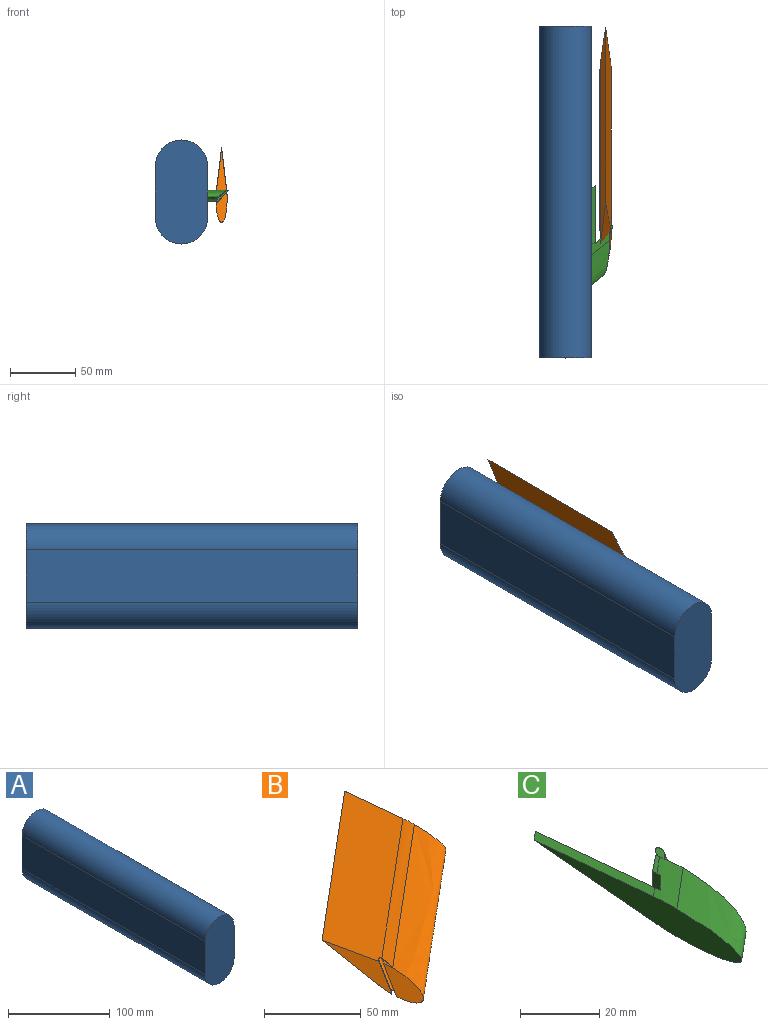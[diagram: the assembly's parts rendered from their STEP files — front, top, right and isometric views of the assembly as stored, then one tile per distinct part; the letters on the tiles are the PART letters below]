
ASSEMBLY  parts=3 mates=2
PART A: 6 faces, bbox 40x255x80 mm
  f0: plane 255x40mm, normal (1,0,0), area 10200mm2, adj f1,f3,f4,f5
  f1: cylinder r=20mm len=255mm, axis (0,1,0), area 16022.1mm2, adj f0,f2,f4,f5
  f2: plane 255x40mm, normal (-1,0,0), area 10200mm2, adj f1,f3,f4,f5
  f3: cylinder r=20mm len=255mm, axis (0,1,0), area 16022.1mm2, adj f0,f2,f4,f5
  f4: plane 80x40mm, normal (0,-1,0), area 2856.6mm2, adj f0,f1,f2,f3
  f5: plane 80x40mm, normal (0,1,0), area 2856.6mm2, adj f0,f1,f2,f3
PART B: 11 faces, bbox 107.4x163.4x11.2 mm
  f0: bspline ~112.18x107.25mm, area 5116.6mm2, adj f1,f2,f4,f5,f7,f8,f9,f10
  f1: bspline ~98.89x91.37mm, area 827.7mm2, adj f0,f2,f3,f4,f8,f9
  f2: plane 33.67x8.66mm, normal (-0.71,0,0.71), area 237.4mm2, adj f0,f1,f8
  f3: plane 124.24x102.95mm, normal (-0.08,0.09,0.99), area 4331.9mm2, adj f1,f4,f6,f7,f9,f10
  f4: plane 74.14x8.6mm, normal (1,0,0), area 393.1mm2, adj f0,f1,f3,f5,f6
  f5: bspline ~107.25x98.38mm, area 900.1mm2, adj f0,f4,f6,f7
  f6: plane 132.31x106.86mm, normal (-0.08,0.09,-0.99), area 4505.1mm2, adj f3,f4,f5,f7
  f7: plane 55.38x8.25mm, normal (-0.71,0,0.71), area 276.3mm2, adj f0,f3,f5,f6,f10
  f8: plane 19.29x9.68mm, normal (-0.59,0.55,-0.59), area 21.3mm2, adj f0,f1,f2,f9
  f9: cylinder r=1mm len=21.6mm, axis (0.39,0.84,0.39), area 65.9mm2, adj f0,f1,f3,f8,f10
  f10: plane 18.81x9.45mm, normal (0.59,-0.55,0.59), area 20.7mm2, adj f0,f3,f7,f9
PART C: 17 faces, bbox 16.7x99.9x11.4 mm
  f0: bspline ~19.96x13.79mm, area 106.4mm2, adj f1,f4,f6,f7,f8,f10,f12,f13
  f1: plane 45.16x3.92mm, normal (-0.08,0.09,0.99), area 128.8mm2, adj f0,f3,f8,f16
  f2: bspline ~19.96x13.79mm, area 40.5mm2, adj f3,f5,f7,f8,f15,f16
  f3: plane 45.16x3.92mm, normal (-0.08,0.09,-0.99), area 128.8mm2, adj f1,f2,f8,f16
  f4: plane 33.64x8.66mm, normal (0.71,0,-0.71), area 237.1mm2, adj f0,f7,f10
  f5: plane 19.01x8.34mm, normal (0.71,0,-0.71), area 67.9mm2, adj f2,f6,f7,f11,f13,f14,f15
  f6: plane 5.99x5.63mm, normal (-0.08,0.09,0.99), area 8.3mm2, adj f0,f5,f13,f14
  f7: bspline ~57.79x13.79mm, area 479.7mm2, adj f0,f2,f4,f5,f8,f10,f11
  f8: plane 74.14x8.6mm, normal (-1,0,0), area 393.1mm2, adj f0,f1,f2,f3,f7
  f9: plane 5x2.89mm, normal (-0.08,0.09,0.99), area 7.8mm2, adj f10,f11,f12
  f10: plane 18.8x9.43mm, normal (0.45,-0.54,0.71), area 17.4mm2, adj f0,f4,f7,f9,f11,f12
  f11: cylinder r=1mm len=21.9mm, axis (-0.39,-0.84,-0.39), area 99mm2, adj f5,f7,f9,f10
  f12: plane 1.77x0.16mm, normal (-0.8,0.1,0.59), area 0mm2, adj f0,f9,f10
  f13: plane 5.74x2.98mm, normal (-1,0,0), area 16.8mm2, adj f0,f5,f6,f14,f15
  f14: plane 5.5x5.5mm, normal (-0.62,0.78,0), area 19.3mm2, adj f5,f6,f13
  f15: plane 8.14x4.78mm, normal (-0.69,0.73,0), area 49.7mm2, adj f0,f2,f5,f13,f16
  f16: plane 44.56x8.14mm, normal (1,0,0), area 182.3mm2, adj f0,f1,f2,f3,f15
PLACE A at identity
PLACE B rot(axis=(0.39,0.83,0.39),100.4deg) t=(30.84,-173.58,-5.72)mm
PLACE C rot(axis=(1,0,0),0.5deg) t=(20,-176.13,-2.97)mm fixed
MATE revolute C.f11 <-> B.f9  axis (-0.39,-0.83,-0.4) through (30.77,-163.97,-2.98)mm
MATE planar A.f0 <-> C.f8  axis (1,0,0) through (20,-127.5,0)mm
